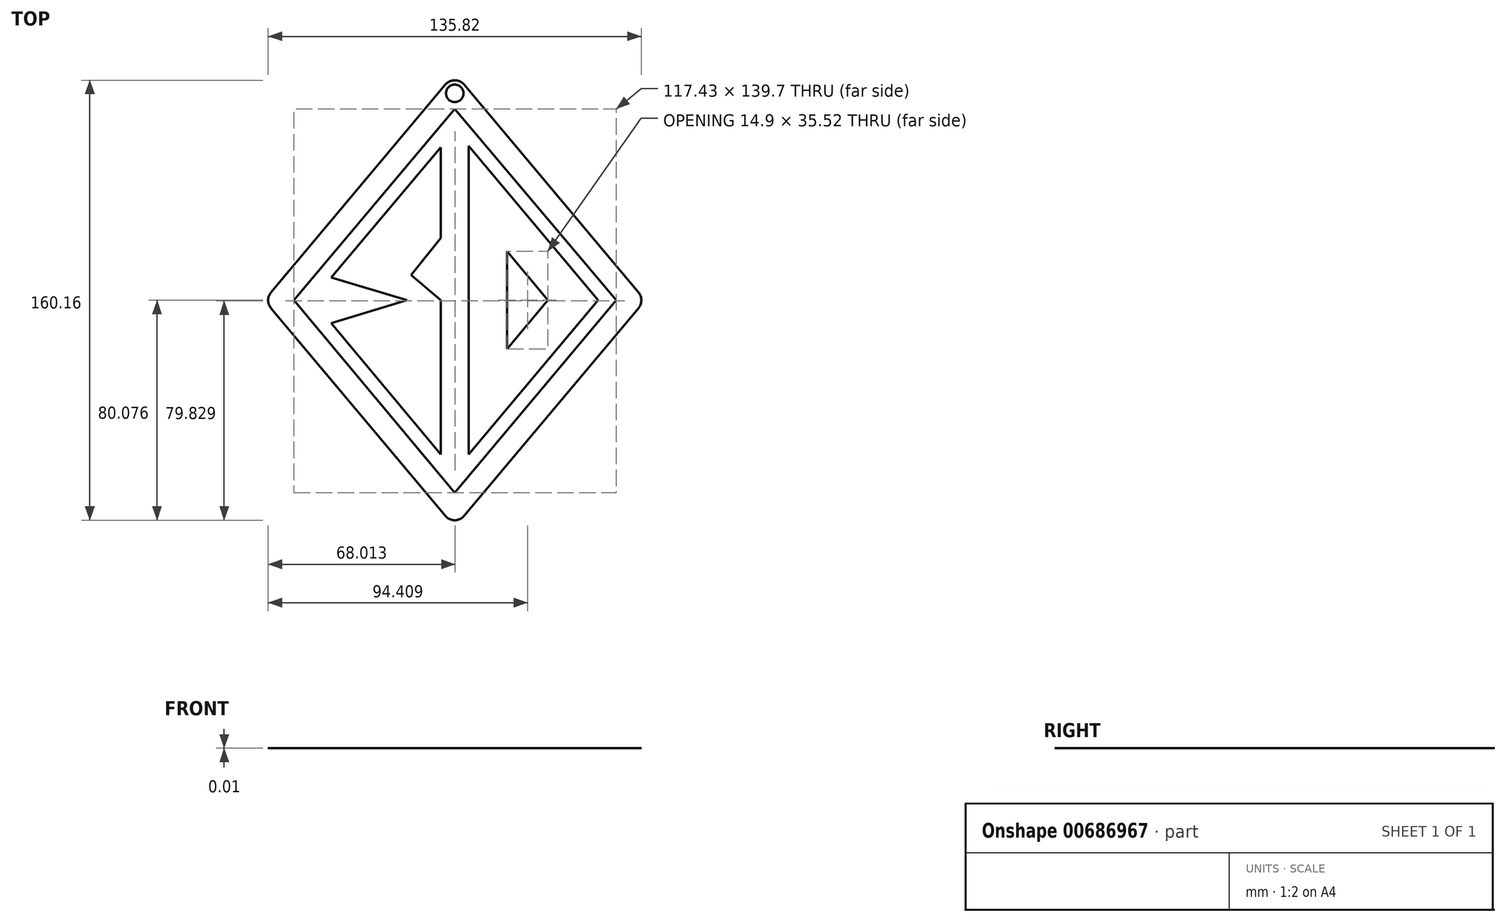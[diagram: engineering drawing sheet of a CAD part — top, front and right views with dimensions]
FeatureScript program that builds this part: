
annotation { "Feature Type Name" : "Feature", "Feature Type Description" : "" }
export const myFeature = defineFeature(function(context is Context, id is Id, definition is map)
    precondition{}
    {
        {
            var Q0;
            Q0=qCreatedBy(makeId("Top.planeOp"),FACE);
            var sketch = newSketch(context, id + "F0", { "sketchPlane" : qUnion([Q0])});
            skLineSegment(sketch, "E0", {"start": v(-3.04, 77.22) * mm, "end": v(-66.5, 1.58) * mm});
            skLineSegment(sketch, "E1", {"start": v(-66.5, -4.13) * mm, "end": v(-3.04, -79.77) * mm});
            skLineSegment(sketch, "E2", {"start": v(3.77, -79.77) * mm, "end": v(67.24, -4.13) * mm});
            skLineSegment(sketch, "E3", {"start": v(67.24, 1.58) * mm, "end": v(3.77, 77.22) * mm});
            skLineSegment(sketch, "E4", {"start": v(-58.24, -1.27) * mm, "end": v(0.37, 68.33) * mm});
            skLineSegment(sketch, "E5", {"start": v(0.37, 68.33) * mm, "end": v(59.19, -1.27) * mm});
            skLineSegment(sketch, "E6", {"start": v(59.19, -1.27) * mm, "end": v(0.37, -71.37) * mm});
            skLineSegment(sketch, "E7", {"start": v(0.37, -71.37) * mm, "end": v(-58.24, -1.27) * mm});
            skLineSegment(sketch, "E8", {"start": v(-4.71, 54.4) * mm, "end": v(-44.6, 7.04) * mm});
            skLineSegment(sketch, "E9", {"start": v(-44.6, 7.04) * mm, "end": v(-16.99, -1.27) * mm});
            skLineSegment(sketch, "E10", {"start": v(-16.99, -1.27) * mm, "end": v(-44.6, -9.67) * mm});
            skLineSegment(sketch, "E11", {"start": v(-44.6, -9.67) * mm, "end": v(-4.71, -57.38) * mm});
            skLineSegment(sketch, "E12", {"start": v(-4.71, -57.38) * mm, "end": v(-4.71, -1.27) * mm});
            skLineSegment(sketch, "E13", {"start": v(-4.71, 54.4) * mm, "end": v(-4.71, 21.4) * mm});
            skLineSegment(sketch, "E14", {"start": v(0.37, 68.33) * mm, "end": v(0.37, -71.37) * mm, "construction": true});
            skLineSegment(sketch, "E15", {"start": v(-58.24, -1.27) * mm, "end": v(59.19, -1.27) * mm, "construction": true});
            skLineSegment(sketch, "E16", {"start": v(-4.71, -1.27) * mm, "end": v(-15.58, 7.88) * mm});
            skLineSegment(sketch, "E17", {"start": v(-15.58, 7.88) * mm, "end": v(-4.71, 21.4) * mm});
            skLineSegment(sketch, "E18", {"start": v(5.45, 54.87) * mm, "end": v(5.45, -57.41) * mm});
            skLineSegment(sketch, "E19", {"start": v(5.45, -57.41) * mm, "end": v(52.56, -1.27) * mm});
            skLineSegment(sketch, "E20", {"start": v(52.56, -1.27) * mm, "end": v(5.45, 54.87) * mm});
            skLineSegment(sketch, "E21", {"start": v(19.42, 16.48) * mm, "end": v(19.42, -19.03) * mm});
            skLineSegment(sketch, "E22", {"start": v(19.42, -19.03) * mm, "end": v(34.32, -1.27) * mm});
            skLineSegment(sketch, "E23", {"start": v(34.32, -1.27) * mm, "end": v(19.42, 16.48) * mm});
            skCircle(sketch, "E24", {"center": v(0.37, 74.04) * mm, "radius": 3.18 * mm});
            skLineSegment(sketch, "E25", {"start": v(0.37, 81.28) * mm, "end": v(0.37, 68.33) * mm, "construction": true});
            skPoint(sketch, "E26.visualSharp", {"position": v(0.37, 81.28) * mm});
            skArc(sketch, "E26.filletArc", {"start": v(3.77, 77.22) * mm, "mid": v(0.37, 78.8) * mm, "end": v(-3.04, 77.22) * mm});
            skPoint(sketch, "E27.visualSharp", {"position": v(-68.9, -1.27) * mm});
            skArc(sketch, "E27.filletArc", {"start": v(-66.5, 1.58) * mm, "mid": v(-67.54, -1.27) * mm, "end": v(-66.5, -4.13) * mm});
            skPoint(sketch, "E28.visualSharp", {"position": v(69.64, -1.27) * mm});
            skArc(sketch, "E28.filletArc", {"start": v(67.24, -4.13) * mm, "mid": v(68.28, -1.27) * mm, "end": v(67.24, 1.58) * mm});
            skPoint(sketch, "E29.visualSharp", {"position": v(0.37, -83.82) * mm});
            skArc(sketch, "E29.filletArc", {"start": v(-3.04, -79.77) * mm, "mid": v(0.37, -81.35) * mm, "end": v(3.77, -79.77) * mm});
            skSolve(sketch);
        }
        {
            var Q0;
            Q0 = qSketchRegion(id + "F0", true);
            var Q1;
            Q1=makeQuery(id+"F0.imprint","IMPRINT",FACE,{"disambiguationData":[TD([[makeQuery(id+"F0.imprint","IMPRINT",EDGE,{"derivedFrom":sQuery(id+"F0.wireOp",EDGE,"E18")}),1.0]])]});
            var Q2;
            Q2=makeQuery(id+"F0.imprint","IMPRINT",FACE,{"disambiguationData":[TD([[makeQuery(id+"F0.imprint","IMPRINT",EDGE,{"derivedFrom":sQuery(id+"F0.wireOp",EDGE,"E8")}),1.0]])]});
            extrude(context, id + "F1", {"entities" : qUnion([Q0, Q1, Q2]), "depth" : 1 / 101.6 * mm, "offsetDistance" : 25.4 * mm});
        }
    });
